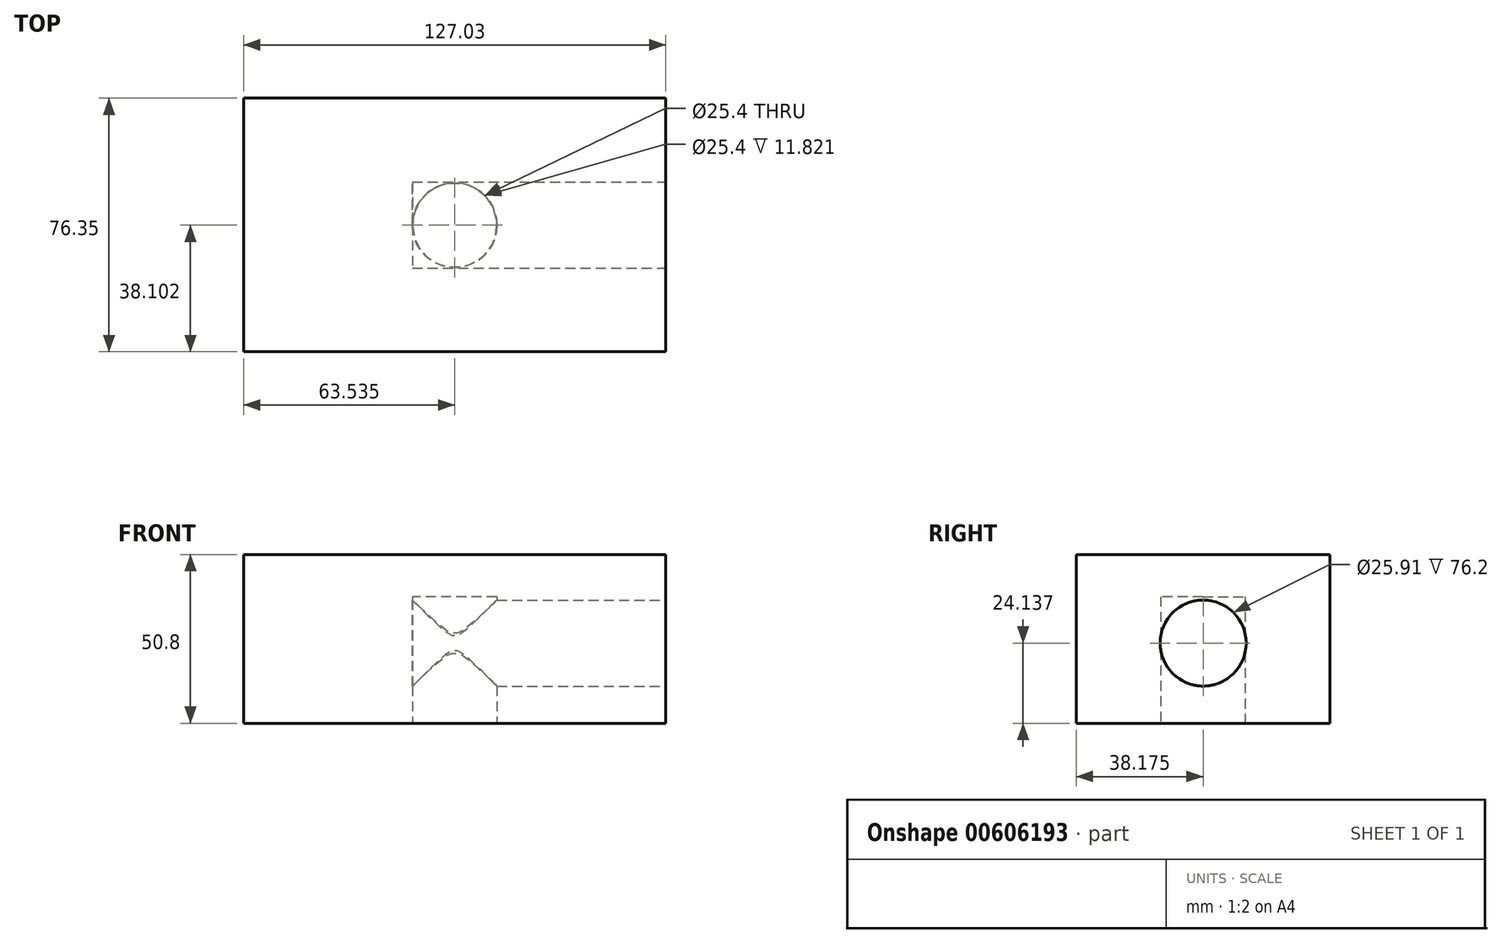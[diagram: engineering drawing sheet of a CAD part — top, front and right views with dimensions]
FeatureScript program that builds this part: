
annotation { "Feature Type Name" : "Feature", "Feature Type Description" : "" }
export const myFeature = defineFeature(function(context is Context, id is Id, definition is map)
    precondition{}
    {
        {
            var Q0;
            Q0=qCreatedBy(makeId("Top.planeOp"),FACE);
            var sketch = newSketch(context, id + "F0", { "sketchPlane" : qUnion([Q0])});
            skLineSegment(sketch, "E0", {"start": v(-33.13, 48.1) * mm, "end": v(93.9, 48.1) * mm});
            skLineSegment(sketch, "E1", {"start": v(93.9, 48.1) * mm, "end": v(93.9, -28.25) * mm});
            skLineSegment(sketch, "E2", {"start": v(93.9, -28.25) * mm, "end": v(-33.13, -28.25) * mm});
            skLineSegment(sketch, "E3", {"start": v(-33.13, -28.25) * mm, "end": v(-33.13, 48.1) * mm});
            skSolve(sketch);
        }
        {
            var Q0;
            Q0=makeQuery(id+"F0.imprint","IMPRINT",FACE,{"disambiguationData":[TD([[makeQuery(id+"F0.imprint","IMPRINT",EDGE,{"derivedFrom":sQuery(id+"F0.wireOp",EDGE,"E0")}),-1.0]])]});
            extrude(context, id + "F1", {"entities" : qUnion([Q0]), "depth" : 50.8 * mm, "offsetDistance" : 25.4 * mm});
        }
        {
            var Q0;
            Q0=makeQuery(id+"F0.imprint","IMPRINT",FACE,{"disambiguationData":[TD([[makeQuery(id+"F0.imprint","IMPRINT",EDGE,{"derivedFrom":sQuery(id+"F0.wireOp",EDGE,"E0")}),-1.0]])]});
            var sketch = newSketch(context, id + "F2", { "sketchPlane" : qUnion([Q0])});
            skCircle(sketch, "E4", {"center": v(30.4, 9.85) * mm, "radius": 12.7 * mm});
            skSolve(sketch);
        }
        {
            var Q0;
            Q0=makeQuery(id+"F2.imprint","IMPRINT",FACE,{"disambiguationData":[TD([[makeQuery(id+"F2.imprint","IMPRINT",EDGE,{"derivedFrom":sQuery(id+"F2.wireOp",EDGE,"E4")}),1.0]])]});
            extrude(context, id + "F3", {"entities" : qUnion([Q0]), "operationType" : NewBodyOperationType.REMOVE, "depth" : 38.1 * mm, "offsetDistance" : 25.4 * mm});
        }
        {
            var Q0;
            Q0=makeQuery(id+"F1.opExtrude","SWEPT_FACE",FACE,{"disambiguationData":[OSD([sQuery(id+"F0.wireOp",EDGE,"E1")])]});
            var sketch = newSketch(context, id + "F4", { "sketchPlane" : qUnion([Q0])});
            skCircle(sketch, "E5", {"center": v(9.92, 24.14) * mm, "radius": 12.95 * mm});
            skPoint(sketch, "E5.centerSnap0", {"position": v(9.92, 0) * mm});
            skSolve(sketch);
        }
        {
            var Q0;
            Q0 = qSketchRegion(id + "F4", true);
            extrude(context, id + "F5", {"entities" : qUnion([Q0]), "operationType" : NewBodyOperationType.REMOVE, "oppositeDirection" : true, "depth" : 76.2 * mm, "offsetDistance" : 25.4 * mm});
        }
    });
